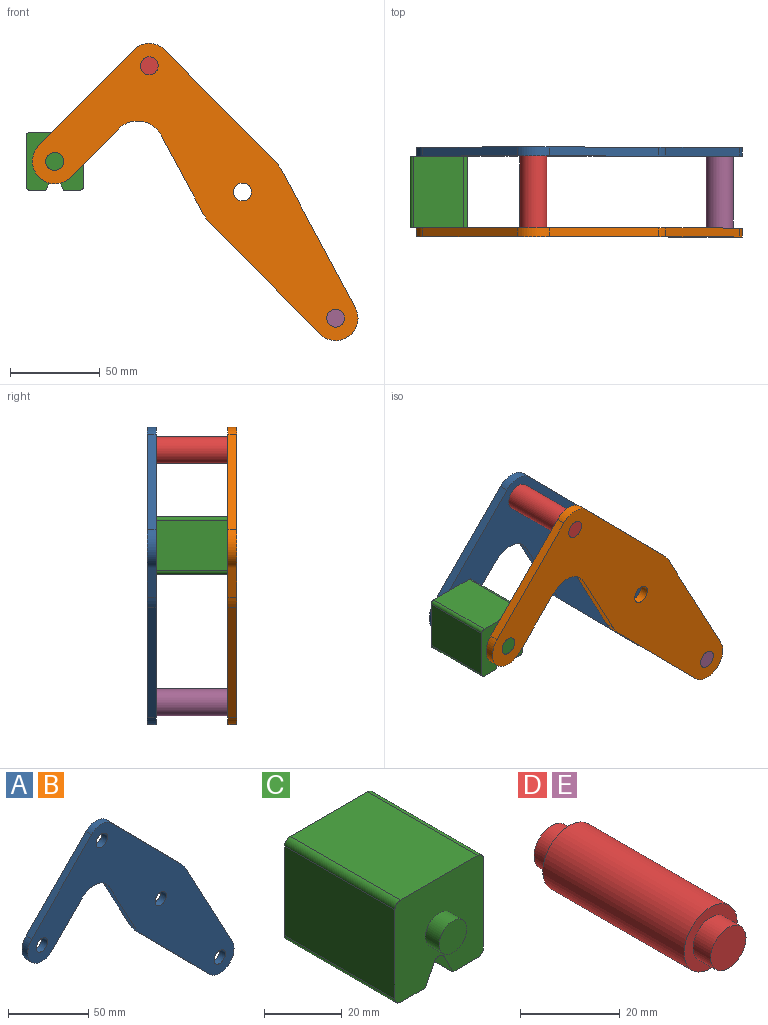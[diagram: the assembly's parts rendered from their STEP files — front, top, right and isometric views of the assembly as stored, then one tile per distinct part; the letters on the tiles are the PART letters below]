
ASSEMBLY  parts=5 mates=3
PART A: 18 faces, bbox 181.7x5x165.8 mm
  f0: plane 43.49x23.35mm, normal (-0.88,0,-0.47), area 246.8mm2, adj f1,f14,f16,f17
  f1: cylinder r=25mm len=5.75mm, axis (0,1,0), area 35.8mm2, adj f0,f2,f16,f17
  f2: plane 61.6x60.87mm, normal (-0.71,0,-0.7), area 433mm2, adj f1,f3,f16,f17
  f3: cylinder r=12.5mm len=21.39mm, axis (0,1,0), area 178.4mm2, adj f2,f4,f16,f17
  f4: plane 76.3x40.96mm, normal (0.88,0,0.47), area 433mm2, adj f3,f5,f16,f17
  f5: cylinder r=25mm len=5.75mm, axis (0,1,0), area 35.8mm2, adj f4,f6,f16,f17
  f6: plane 61.6x60.87mm, normal (0.71,0,0.7), area 433mm2, adj f5,f7,f16,f17
  f7: cylinder r=12.5mm len=17.78mm, axis (0,1,0), area 98.9mm2, adj f6,f8,f16,f17
  f8: plane 53.35x52.71mm, normal (-0.71,0,0.7), area 375mm2, adj f7,f9,f16,f17
  f9: cylinder r=12.5mm len=21.39mm, axis (0,1,0), area 196.3mm2, adj f8,f10,f16,f17
  f10: plane 26.86x26.54mm, normal (0.71,0,-0.7), area 188.8mm2, adj f9,f14,f16,f17
  f11: cylinder r=5mm len=10mm, axis (0,1,0), area 157.1mm2, adj f16,f17
  f12: cylinder r=5mm len=10mm, axis (0,1,0), area 157.1mm2, adj f16,f17
  f13: cylinder r=5mm len=10mm, axis (0,1,0), area 157.1mm2, adj f16,f17
  f14: cylinder r=15mm len=23.89mm, axis (0,1,0), area 140.2mm2, adj f0,f10,f16,f17
  f15: cylinder r=5mm len=10mm, axis (0,1,0), area 157.1mm2, adj f16,f17
  f16: plane 181.66x165.78mm, normal (0,-1,0), area 8710.1mm2, adj f0,f1,f2,f3,f4,f5,f6,f7
  f17: plane 181.66x165.78mm, normal (0,1,0), area 8710.1mm2, adj f0,f1,f2,f3,f4,f5,f6,f7
PART B: same geometry as A
PART C: 18 faces, bbox 32.1x50x32.1 mm
  f0: plane 40x28.08mm, normal (1,0,0), area 1123.1mm2, adj f4,f10,f13,f14
  f1: plane 40x9.04mm, normal (0,0,-1), area 361.6mm2, adj f2,f4,f10,f14
  f2: plane 40x6.42mm, normal (-0.89,0,-0.45), area 287.2mm2, adj f1,f4,f10,f15
  f3: plane 40x6.42mm, normal (0.89,0,-0.45), area 287.2mm2, adj f4,f5,f10,f15
  f4: plane 32.08x32.08mm, normal (0,-1,0), area 900.6mm2, adj f0,f1,f2,f3,f5,f6,f7,f9
  f5: plane 40x9.04mm, normal (0,0,-1), area 361.6mm2, adj f3,f4,f10,f16
  f6: plane 40x28.08mm, normal (0,0,1), area 1123.1mm2, adj f4,f10,f13,f17
  f7: plane 40x28.08mm, normal (-1,0,0), area 1123.1mm2, adj f4,f10,f16,f17
  f8: plane 10x10mm, normal (0,-1,0), area 78.5mm2, adj f9
  f9: cylinder r=5mm len=10mm, axis (0,1,0), area 157.1mm2, adj f4,f8
  f10: plane 32.08x32.08mm, normal (0,1,0), area 900.6mm2, adj f0,f1,f2,f3,f5,f6,f7,f12
  f11: plane 10x10mm, normal (0,1,0), area 78.5mm2, adj f12
  f12: cylinder r=5mm len=10mm, axis (0,-1,0), area 157.1mm2, adj f10,f11
  f13: cylinder r=2mm len=40mm, axis (0,1,0), area 125.7mm2, adj f0,f4,f6,f10
  f14: cylinder r=2mm len=40mm, axis (0,-1,0), area 125.7mm2, adj f0,f1,f4,f10
  f15: cylinder r=2mm len=40mm, axis (0,1,0), area 177.1mm2, adj f2,f3,f4,f10
  f16: cylinder r=2mm len=40mm, axis (0,1,0), area 125.7mm2, adj f4,f5,f7,f10
  f17: cylinder r=2mm len=40mm, axis (0,-1,0), area 125.7mm2, adj f4,f6,f7,f10
PART D: 7 faces, bbox 15x50x15 mm
  f0: cylinder r=7.5mm len=40mm, axis (0,-1,0), area 1885mm2, adj f2,f5
  f1: cylinder r=5mm len=10mm, axis (0,1,0), area 157.1mm2, adj f2,f3
  f2: plane 15x15mm, normal (0,-1,0), area 98.2mm2, adj f0,f1
  f3: plane 10x10mm, normal (0,-1,0), area 78.5mm2, adj f1
  f4: cylinder r=5mm len=10mm, axis (0,-1,0), area 157.1mm2, adj f5,f6
  f5: plane 15x15mm, normal (0,1,0), area 98.2mm2, adj f0,f4
  f6: plane 10x10mm, normal (0,1,0), area 78.5mm2, adj f4
PART E: same geometry as D
PLACE A t=(0,25,0)mm
PLACE B t=(0,-20,0)mm fixed
PLACE C t=(0,-20,0)mm
PLACE D t=(0,-20,0)mm
PLACE E t=(103.95,-20,-140.78)mm
MATE fastened A.f7 <-> D.f0  axis (0,-1,0) through (-51.98,20,70.39)mm
MATE revolute B.f9 <-> C.f9  axis (0,-1,0) through (-104.69,-25,17.04)mm
MATE fastened B.f3 <-> E.f0  axis (0,-1,0) through (51.98,-25,-70.39)mm
